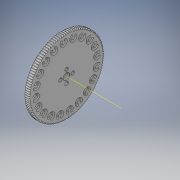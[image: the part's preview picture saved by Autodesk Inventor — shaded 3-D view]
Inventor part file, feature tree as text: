
AUTODESK INVENTOR PART (.ipt)
format: ipt  version: 2016 SP2 (Build 200236200, 236)  size: 5,402,624 bytes
history: native  units: in
note: dims shown in document units (in); Inventor stores cm internally (conversion verified against a paired STEP export)
features: extrude x3, sketch x3, other x1, pattern_circular x1, imported_body x1
ambient origin geometry x8: Origin, YZ Plane, XZ Plane, XY Plane, X Axis, Y Axis, Z Axis, Center Point
bodies: Solid1 (feature_tree)
feature tree (9):
  extrude  "Extrusion1"  Depth=0.25in TaperAngle=0.0deg
  other  "Work Axis1"
  extrude  "Extrusion2"  Depth=7.874in TaperAngle=360.0deg
  extrude  "Extrusion3"  [1 undecoded]
  pattern_circular  "Circular Pattern2"  [2 undecoded]
  sketch  "Sketch1"  dims[d0=0.25in d1=0.0in d5=0.25in d6=0.0in]
  sketch  "Sketch2"  dims[d7=0.25in d8=0.0in d9=7.874in d10=360.0deg]
  sketch  "Sketch3"
  imported_body  "Base1"
note: 3 required parameter values undecoded (feature->parameter linkage not recoverable at this tier; creation-order binding heuristic only, values carry confidence <= 0.55)
